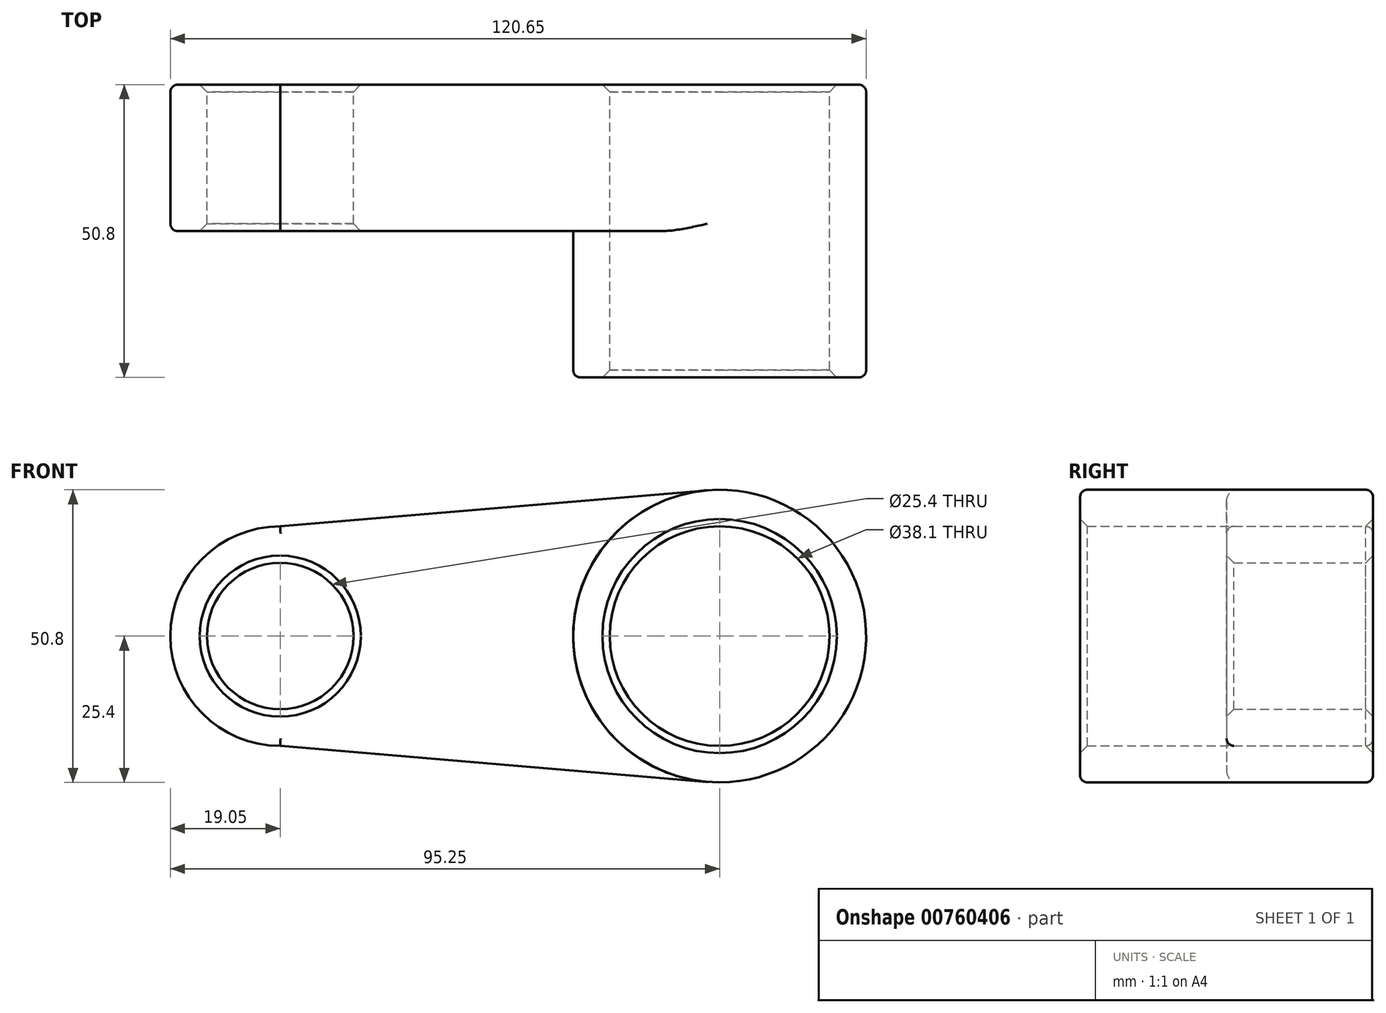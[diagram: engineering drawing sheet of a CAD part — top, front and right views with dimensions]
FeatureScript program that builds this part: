
annotation { "Feature Type Name" : "Feature", "Feature Type Description" : "" }
export const myFeature = defineFeature(function(context is Context, id is Id, definition is map)
    precondition{}
    {
        {
            var Q0;
            Q0=qCreatedBy(makeId("Front.planeOp"),FACE);
            var sketch = newSketch(context, id + "F0", { "sketchPlane" : qUnion([Q0])});
            skCircle(sketch, "E0", {"center": v(0, 0) * mm, "radius": 19.05 * mm});
            skCircle(sketch, "E1", {"center": v(76.2, 0) * mm, "radius": 25.4 * mm});
            skCircle(sketch, "E2", {"center": v(0, 0) * mm, "radius": 12.7 * mm});
            skCircle(sketch, "E3", {"center": v(76.2, 0) * mm, "radius": 19.05 * mm});
            skLineSegment(sketch, "E4", {"start": v(0, 19.05) * mm, "end": v(74.06, 25.3) * mm});
            skLineSegment(sketch, "E5", {"start": v(0, -19.05) * mm, "end": v(74.06, -25.3) * mm});
            skSolve(sketch);
        }
        {
            var Q0;
            Q0 = qSketchRegion(id + "F0", true);
            extrude(context, id + "F1", {"entities" : qUnion([Q0]), "depth" : 25.4 * mm, "offsetDistance" : 25.4 * mm});
        }
        {
            var Q0;
            Q0=makeQuery(id+"F0.imprint","IMPRINT",FACE,{"disambiguationData":[TD([[makeQuery(id+"F0.imprint","IMPRINT",EDGE,{"derivedFrom":sQuery(id+"F0.wireOp",EDGE,"E3")}),-1.0]])]});
            extrude(context, id + "F2", {"entities" : qUnion([Q0]), "operationType" : NewBodyOperationType.ADD, "depth" : 50.8 * mm, "offsetDistance" : 25.4 * mm});
        }
        {
            var Q0;
            Q0=makeQuery(id+"F2.opExtrude","CAP_EDGE",EDGE,{"disambiguationData":[OSD([sQuery(id+"F0.wireOp",EDGE,"E1")])],"isStart":false});
            var Q1;
            Q1=makeQuery(id+"F1.opExtrude","CAP_EDGE",EDGE,{"disambiguationData":[OSD([sQuery(id+"F0.wireOp",EDGE,"E4")])],"isStart":true});
            var Q2;
            Q2=makeQuery(id+"F1.opExtrude","CAP_EDGE",EDGE,{"disambiguationData":[OSD([sQuery(id+"F0.wireOp",EDGE,"E0")])],"isStart":true});
            var Q3;
            Q3=makeQuery(id+"F1.opExtrude","CAP_EDGE",EDGE,{"disambiguationData":[OSD([sQuery(id+"F0.wireOp",EDGE,"E0")])],"isStart":false});
            fillet(context, id + "F3", {"entities" : qUnion([Q0, Q1, Q2, Q3]), "radius" : 1.27 * mm, "tangentPropagation" : true, "allowEdgeOverflow" : false});
        }
        {
            var Q0;
            Q0=makeQuery(id+"F1.opExtrude","CAP_EDGE",EDGE,{"disambiguationData":[OSD([sQuery(id+"F0.wireOp",EDGE,"E2")])],"isStart":false});
            var Q1;
            Q1=makeQuery(id+"F2.opExtrude","CAP_EDGE",EDGE,{"disambiguationData":[OSD([sQuery(id+"F0.wireOp",EDGE,"E3")])],"isStart":false});
            var Q2;
            Q2=makeQuery(id+"F1.opExtrude","CAP_EDGE",EDGE,{"disambiguationData":[OSD([sQuery(id+"F0.wireOp",EDGE,"E3")])],"isStart":true});
            var Q3;
            Q3=makeQuery(id+"F1.opExtrude","CAP_EDGE",EDGE,{"disambiguationData":[OSD([sQuery(id+"F0.wireOp",EDGE,"E2")])],"isStart":true});
            chamfer(context, id + "F4", {"entities" : qUnion([Q0, Q1, Q2, Q3]), "width" : 1.27 * mm, "tangentPropagation" : true});
        }
    });
